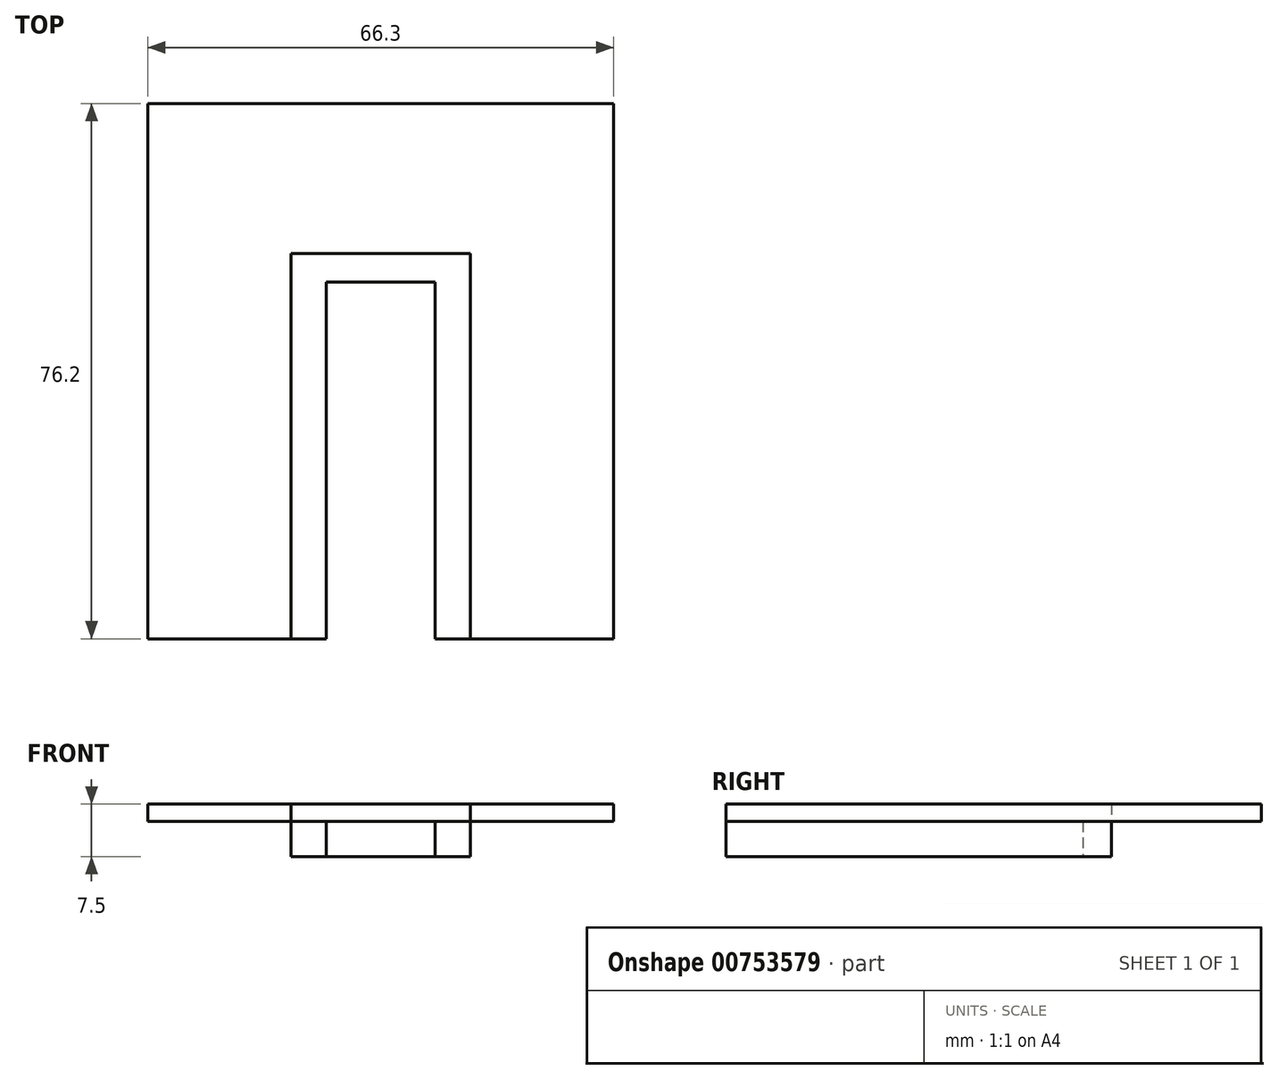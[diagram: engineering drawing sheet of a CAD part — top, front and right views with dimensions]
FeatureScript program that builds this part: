
annotation { "Feature Type Name" : "Feature", "Feature Type Description" : "" }
export const myFeature = defineFeature(function(context is Context, id is Id, definition is map)
    precondition{}
    {
        {
            var Q0;
            Q0=qCreatedBy(makeId("Top.planeOp"),FACE);
            var sketch = newSketch(context, id + "F0", { "sketchPlane" : qUnion([Q0])});
            skLineSegment(sketch, "E0", {"start": v(-35.6, 35.78) * mm, "end": v(-35.6, 5.71) * mm});
            skLineSegment(sketch, "E1", {"start": v(-35.6, 5.71) * mm, "end": v(-30.6, 5.71) * mm});
            skLineSegment(sketch, "E2", {"start": v(-30.6, 5.71) * mm, "end": v(-30.6, 56.51) * mm});
            skLineSegment(sketch, "E3", {"start": v(-30.6, 56.51) * mm, "end": v(-15.1, 56.51) * mm});
            skLineSegment(sketch, "E4", {"start": v(-22.86, 48.77) * mm, "end": v(-22.86, 0) * mm, "construction": true});
            skPoint(sketch, "E4.startSnap0", {"position": v(-22.86, 56.51) * mm});
            skLineSegment(sketch, "E5.MirrorCS", {"start": v(-15.1, 56.51) * mm, "end": v(-30.6, 56.51) * mm});
            skLineSegment(sketch, "E6.MirrorCS", {"start": v(-15.1, 5.71) * mm, "end": v(-15.1, 56.51) * mm});
            skLineSegment(sketch, "E7.MirrorCS", {"start": v(-10.1, 35.78) * mm, "end": v(-10.1, 5.71) * mm});
            skLineSegment(sketch, "E8.MirrorCS", {"start": v(-10.1, 5.71) * mm, "end": v(-15.1, 5.71) * mm});
            skLineSegment(sketch, "E9", {"start": v(-35.6, 35.78) * mm, "end": v(-35.6, 60.56) * mm});
            skLineSegment(sketch, "E10", {"start": v(-35.6, 60.56) * mm, "end": v(-10.1, 60.56) * mm});
            skLineSegment(sketch, "E11", {"start": v(-10.1, 60.56) * mm, "end": v(-10.1, 35.78) * mm});
            skSolve(sketch);
        }
        {
            var Q0;
            Q0=makeQuery(id+"F0.imprint","IMPRINT",FACE,{"disambiguationData":[TD([[makeQuery(id+"F0.imprint","IMPRINT",EDGE,{"derivedFrom":sQuery(id+"F0.wireOp",EDGE,"E0")}),1.0]])]});
            extrude(context, id + "F1", {"entities" : qUnion([Q0]), "depth" : 5 * mm, "offsetDistance" : 25.4 * mm});
        }
        {
            var Q0;
            Q0=makeQuery(id+"F1.opExtrude","CAP_FACE",FACE,{"disambiguationData":[OSD([sQuery(id+"F0.wireOp",EDGE,"E0"),sQuery(id+"F0.wireOp",EDGE,"E1"),sQuery(id+"F0.wireOp",EDGE,"E2"),sQuery(id+"F0.wireOp",EDGE,"E5.MirrorCS"),sQuery(id+"F0.wireOp",EDGE,"E6.MirrorCS"),sQuery(id+"F0.wireOp",EDGE,"E7.MirrorCS"),sQuery(id+"F0.wireOp",EDGE,"E8.MirrorCS"),sQuery(id+"F0.wireOp",EDGE,"E9"),sQuery(id+"F0.wireOp",EDGE,"E10"),sQuery(id+"F0.wireOp",EDGE,"E11")])],"isStart":false});
            var sketch = newSketch(context, id + "F2", { "sketchPlane" : qUnion([Q0])});
            skLineSegment(sketch, "E12", {"start": v(-30.6, 5.71) * mm, "end": v(-56, 5.71) * mm});
            skLineSegment(sketch, "E13", {"start": v(-56, 5.71) * mm, "end": v(-56, 73.74) * mm});
            skPoint(sketch, "E14.endSnap0", {"position": v(-22.86, 60.56) * mm});
            skLineSegment(sketch, "E15", {"start": v(-22.86, 56.51) * mm, "end": v(-22.86, 81.91) * mm, "construction": true});
            skLineSegment(sketch, "E16", {"start": v(-56, 73.74) * mm, "end": v(-56, 81.91) * mm});
            skLineSegment(sketch, "E17", {"start": v(-56, 81.91) * mm, "end": v(-22.86, 81.91) * mm});
            skLineSegment(sketch, "E18.MirrorCS", {"start": v(10.3, 81.91) * mm, "end": v(-22.86, 81.91) * mm});
            skLineSegment(sketch, "E19.MirrorCS", {"start": v(10.3, 73.74) * mm, "end": v(10.3, 81.91) * mm});
            skLineSegment(sketch, "E20.MirrorCS", {"start": v(10.3, 5.71) * mm, "end": v(10.3, 73.74) * mm});
            skLineSegment(sketch, "E21.MirrorCS", {"start": v(-15.1, 5.71) * mm, "end": v(10.3, 5.71) * mm});
            skSolve(sketch);
        }
        {
            var Q0;
            {var subQ5=sQuery(id+"F2.wireOp",EDGE,"E13");Q0=makeQuery(id+"F2.imprint","IMPRINT",FACE,{"disambiguationData":[TD([[makeQuery(id+"F2.imprint","IMPRINT",EDGE,{"derivedFrom":subQ5}),-1.0]])]});}
            extrude(context, id + "F3", {"entities" : qUnion([Q0]), "depth" : 2.5 * mm, "offsetDistance" : 25.4 * mm});
        }
    });
